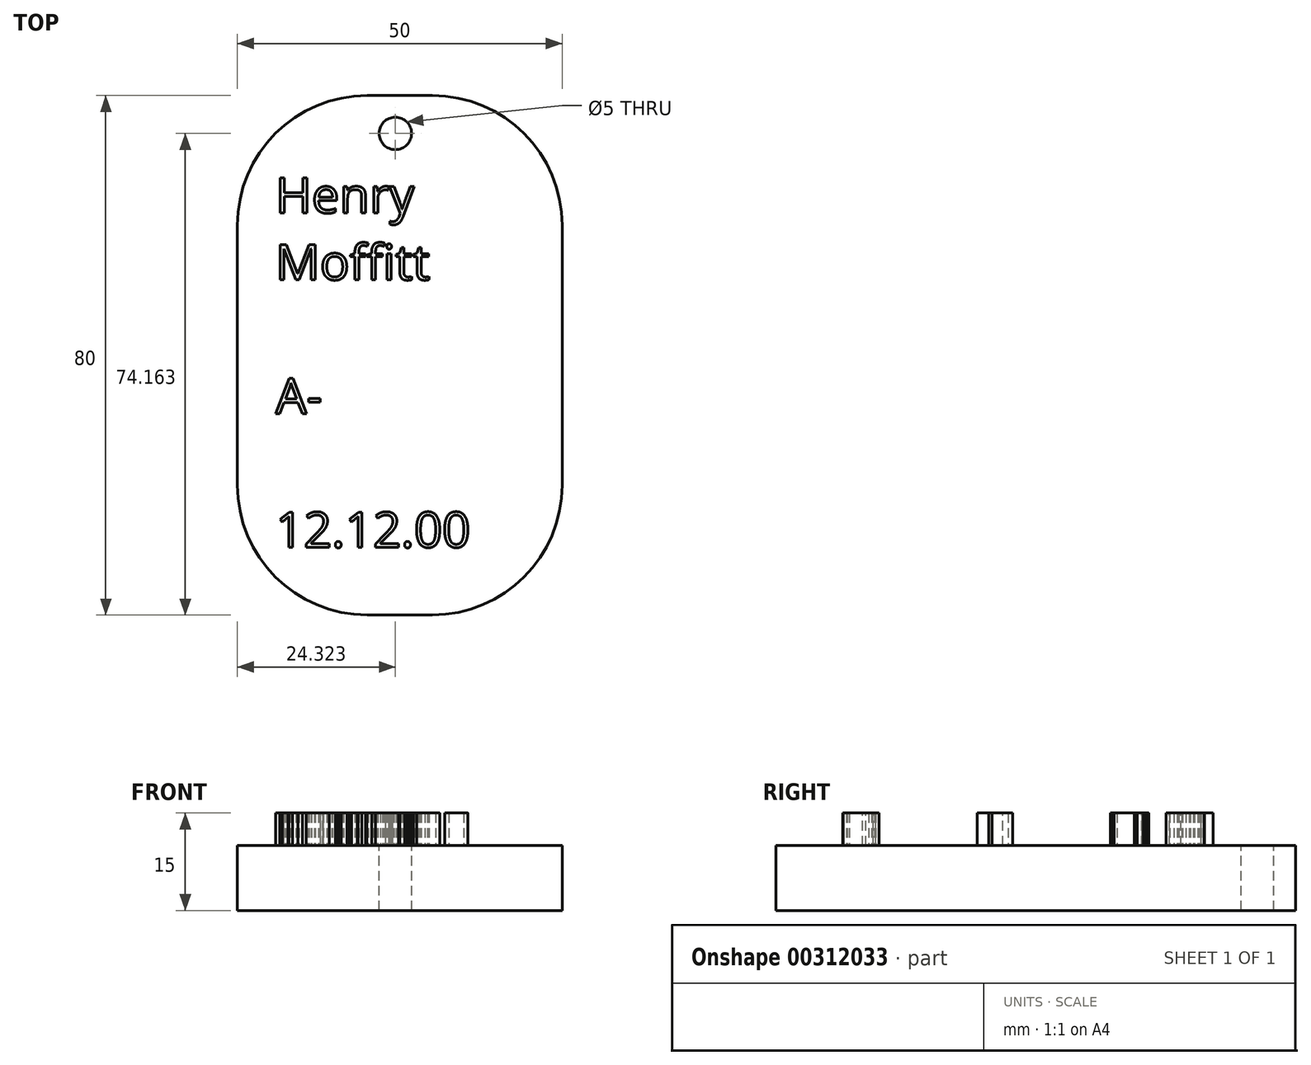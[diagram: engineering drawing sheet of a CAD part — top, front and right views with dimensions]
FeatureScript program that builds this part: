
annotation { "Feature Type Name" : "Feature", "Feature Type Description" : "" }
export const myFeature = defineFeature(function(context is Context, id is Id, definition is map)
    precondition{}
    {
        {
            var Q0;
            Q0=qCreatedBy(makeId("Top.planeOp"),FACE);
            var sketch = newSketch(context, id + "F0", { "sketchPlane" : qUnion([Q0])});
            skLineSegment(sketch, "E0.bottom", {"start": v(-70.17, 69.21) * mm, "end": v(-20.17, 69.21) * mm});
            skLineSegment(sketch, "E0.top", {"start": v(-70.17, -10.79) * mm, "end": v(-20.17, -10.79) * mm});
            skLineSegment(sketch, "E0.left", {"start": v(-70.17, 69.21) * mm, "end": v(-70.17, -10.79) * mm});
            skLineSegment(sketch, "E0.right", {"start": v(-20.17, 69.21) * mm, "end": v(-20.17, -10.79) * mm});
            skSolve(sketch);
        }
        {
            var Q0;
            Q0=makeQuery(id+"F0.imprint","IMPRINT",FACE,{"disambiguationData":[TD([[makeQuery(id+"F0.imprint","IMPRINT",EDGE,{"derivedFrom":sQuery(id+"F0.wireOp",EDGE,"E0.bottom")}),-1.0]])]});
            extrude(context, id + "F1", {"entities" : qUnion([Q0]), "depth" : 10 * mm});
        }
        {
            var Q0;
            Q0=makeQuery(id+"F1.opExtrude","SWEPT_EDGE",EDGE,{"disambiguationData":[OSD([sQuery(id+"F0.wireOp",EDGE,"E0.top"),sQuery(id+"F0.wireOp",EDGE,"E0.left")])]});
            var Q1;
            Q1=makeQuery(id+"F1.opExtrude","SWEPT_EDGE",EDGE,{"disambiguationData":[OSD([sQuery(id+"F0.wireOp",EDGE,"E0.top"),sQuery(id+"F0.wireOp",EDGE,"E0.right")])]});
            var Q2;
            Q2=makeQuery(id+"F1.opExtrude","SWEPT_EDGE",EDGE,{"disambiguationData":[OSD([sQuery(id+"F0.wireOp",EDGE,"E0.bottom"),sQuery(id+"F0.wireOp",EDGE,"E0.right")])]});
            var Q3;
            Q3=makeQuery(id+"F1.opExtrude","SWEPT_EDGE",EDGE,{"disambiguationData":[OSD([sQuery(id+"F0.wireOp",EDGE,"E0.bottom"),sQuery(id+"F0.wireOp",EDGE,"E0.left")])]});
            fillet(context, id + "F2", {"entities" : qUnion([Q0, Q1, Q2, Q3]), "radius" : 20 * mm, "tangentPropagation" : true, "allowEdgeOverflow" : false});
        }
        {
            var Q0;
            Q0=makeQuery(id+"F1.opExtrude","CAP_FACE",FACE,{"disambiguationData":[OSD([sQuery(id+"F0.wireOp",EDGE,"E0.bottom"),sQuery(id+"F0.wireOp",EDGE,"E0.top"),sQuery(id+"F0.wireOp",EDGE,"E0.left"),sQuery(id+"F0.wireOp",EDGE,"E0.right")])],"isStart":false});
            var sketch = newSketch(context, id + "F3", { "sketchPlane" : qUnion([Q0])});
            skPoint(sketch, "E1", {"position": v(-45.85, 63.37) * mm});
            skSolve(sketch);
        }
        {
            var Q0;
            Q0=sQuery(id+"F3.wireOp",VERTEX,"E1");
            var Q1;
            Q1=makeQuery(id+"F1.opExtrude","SWEPT_BODY",BODY,{"disambiguationData":[OSD([sQuery(id+"F0.wireOp",EDGE,"E0.bottom"),sQuery(id+"F0.wireOp",EDGE,"E0.top"),sQuery(id+"F0.wireOp",EDGE,"E0.left"),sQuery(id+"F0.wireOp",EDGE,"E0.right")])]});
            hole(context, id + "F4", {"style" : HoleStyle.SIMPLE, "endStyle" : HoleEndStyle.THROUGH, "holeDiameter" : 5 * mm, "tappedDepth" : 12 * mm, "tapClearance" : 3, "locations" : qUnion([Q0]), "scope" : qUnion([Q1])});
        }
        {
            var Q0;
            Q0=makeQuery(id+"F1.opExtrude","CAP_FACE",FACE,{"disambiguationData":[OSD([sQuery(id+"F0.wireOp",EDGE,"E0.bottom"),sQuery(id+"F0.wireOp",EDGE,"E0.top"),sQuery(id+"F0.wireOp",EDGE,"E0.left"),sQuery(id+"F0.wireOp",EDGE,"E0.right")])],"isStart":false});
            var sketch = newSketch(context, id + "F5", { "sketchPlane" : qUnion([Q0])});
            skText(sketch, "E2", { "text": "Henry\nMoffitt\n\nA-\n\n12.12.00", "fontName": "OpenSans-Regular.ttf"});
            skPoint(sketch, "E2.firstSnap0", {"position": v(-64.3, 63.36) * mm});
            const initialGuessF5  = {"E2": [-0.0643, 0.05111, 1, 0, 0.00545]};
            skSetInitialGuess(sketch, initialGuessF5);
            skSolve(sketch);
        }
        {
            var Q0;
            Q0 = qSketchRegion(id + "F5", true);
            extrude(context, id + "F6", {"entities" : qUnion([Q0]), "operationType" : NewBodyOperationType.ADD, "depth" : 5 * mm});
        }
    });
